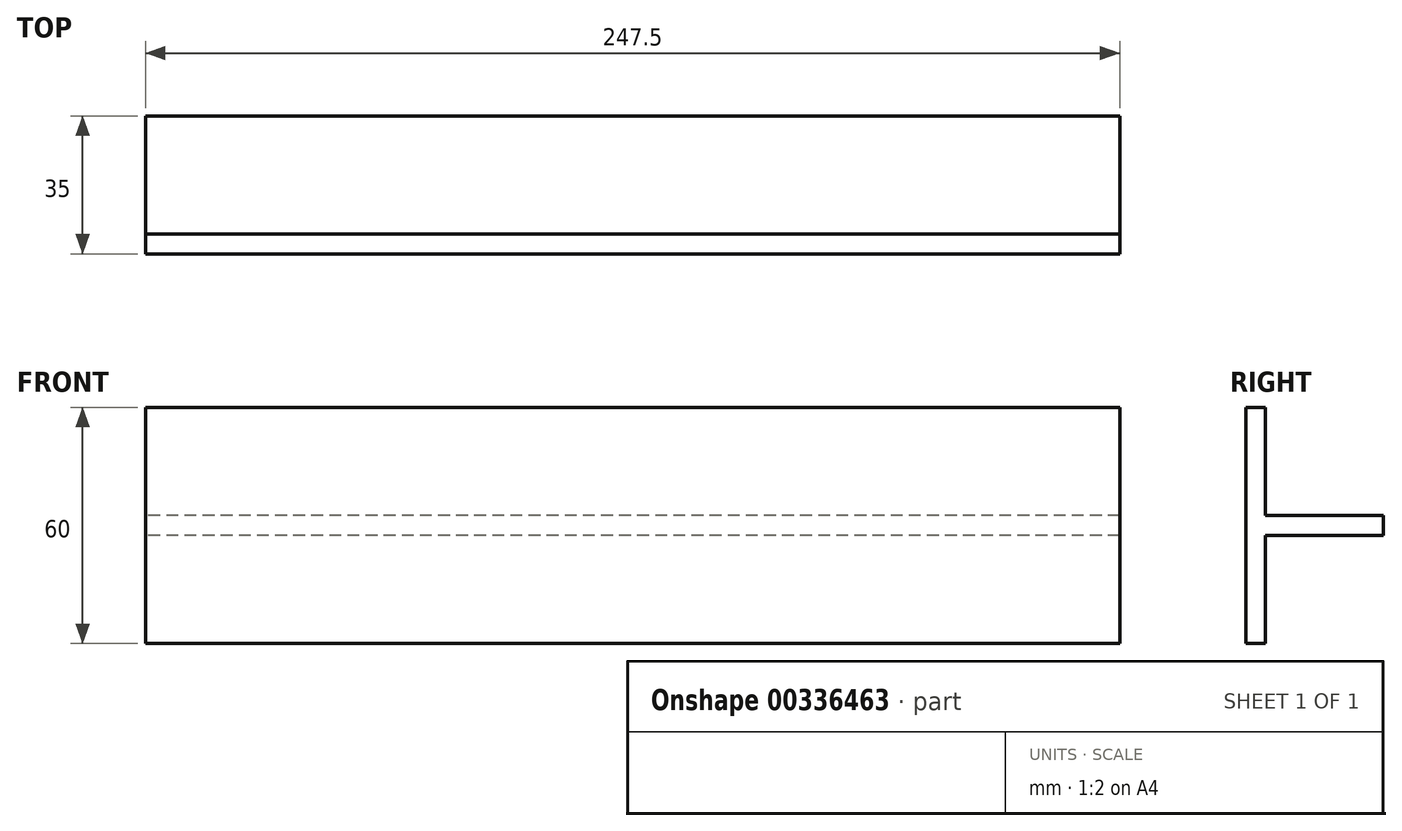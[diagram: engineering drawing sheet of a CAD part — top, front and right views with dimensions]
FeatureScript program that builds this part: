
annotation { "Feature Type Name" : "Feature", "Feature Type Description" : "" }
export const myFeature = defineFeature(function(context is Context, id is Id, definition is map)
    precondition{}
    {
        {
            var Q0;
            Q0=qCreatedBy(makeId("Right.planeOp"),FACE);
            var sketch = newSketch(context, id + "F0", { "sketchPlane" : qUnion([Q0])});
            skLineSegment(sketch, "E0", {"start": v(0, -30) * mm, "end": v(5, -30) * mm});
            skLineSegment(sketch, "E1", {"start": v(5, -30) * mm, "end": v(5, -2.5) * mm});
            skLineSegment(sketch, "E2", {"start": v(5, -2.5) * mm, "end": v(35, -2.5) * mm});
            skLineSegment(sketch, "E3", {"start": v(35, -2.5) * mm, "end": v(35, 0) * mm});
            skLineSegment(sketch, "E4", {"start": v(0, -30) * mm, "end": v(0, 0) * mm});
            skLineSegment(sketch, "E5.MirrorCS", {"start": v(35, 2.5) * mm, "end": v(35, 0) * mm});
            skLineSegment(sketch, "E6.MirrorCS", {"start": v(0, 30) * mm, "end": v(5, 30) * mm});
            skLineSegment(sketch, "E7.MirrorCS", {"start": v(5, 2.5) * mm, "end": v(35, 2.5) * mm});
            skLineSegment(sketch, "E8.MirrorCS", {"start": v(5, 30) * mm, "end": v(5, 2.5) * mm});
            skLineSegment(sketch, "E9.MirrorCS", {"start": v(0, 30) * mm, "end": v(0, 0) * mm});
            skSolve(sketch);
        }
        {
            var Q0;
            Q0=makeQuery(id+"F0.imprint","IMPRINT",FACE,{"disambiguationData":[TD([[makeQuery(id+"F0.imprint","IMPRINT",EDGE,{"derivedFrom":sQuery(id+"F0.wireOp",EDGE,"E0")}),1.0]])]});
            extrude(context, id + "F1", {"entities" : qUnion([Q0]), "endBound" : BoundingType.SYMMETRIC, "depth" : (495 / 2) * mm});
        }
    });
